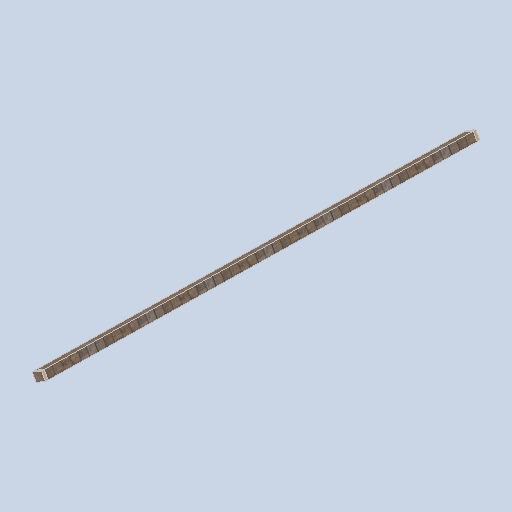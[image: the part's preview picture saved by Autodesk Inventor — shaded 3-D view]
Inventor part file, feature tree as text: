
AUTODESK INVENTOR PART (.ipt)
format: ipt  version: 2024.2 (Build 282272000, 272)  size: 133,120 bytes
history: native  units: in
note: dims shown in document units (in); Inventor stores cm internally (conversion verified against a paired STEP export)
features: sketch x4, other x3, plane x2
ambient origin geometry x8: Origin, YZ Plane, XZ Plane, XY Plane, X Axis, Y Axis, Z Axis, Center Point
bodies: Solid1 (feature_tree)
feature tree (9):
  other  "support_beam_segment_0105_MIR.ipt"
  other  "Solid1::support_beam_segment_0105_MIR.ipt"
  other  "TaggingFeature1"
  sketch  "Sketch1"  dims[d0=0.3937in]
  sketch  "Sketch2"
  sketch  "Sketch3"
  sketch  "Sketch4"
  plane  "Work Plane1"
  plane  "Work Plane2"
